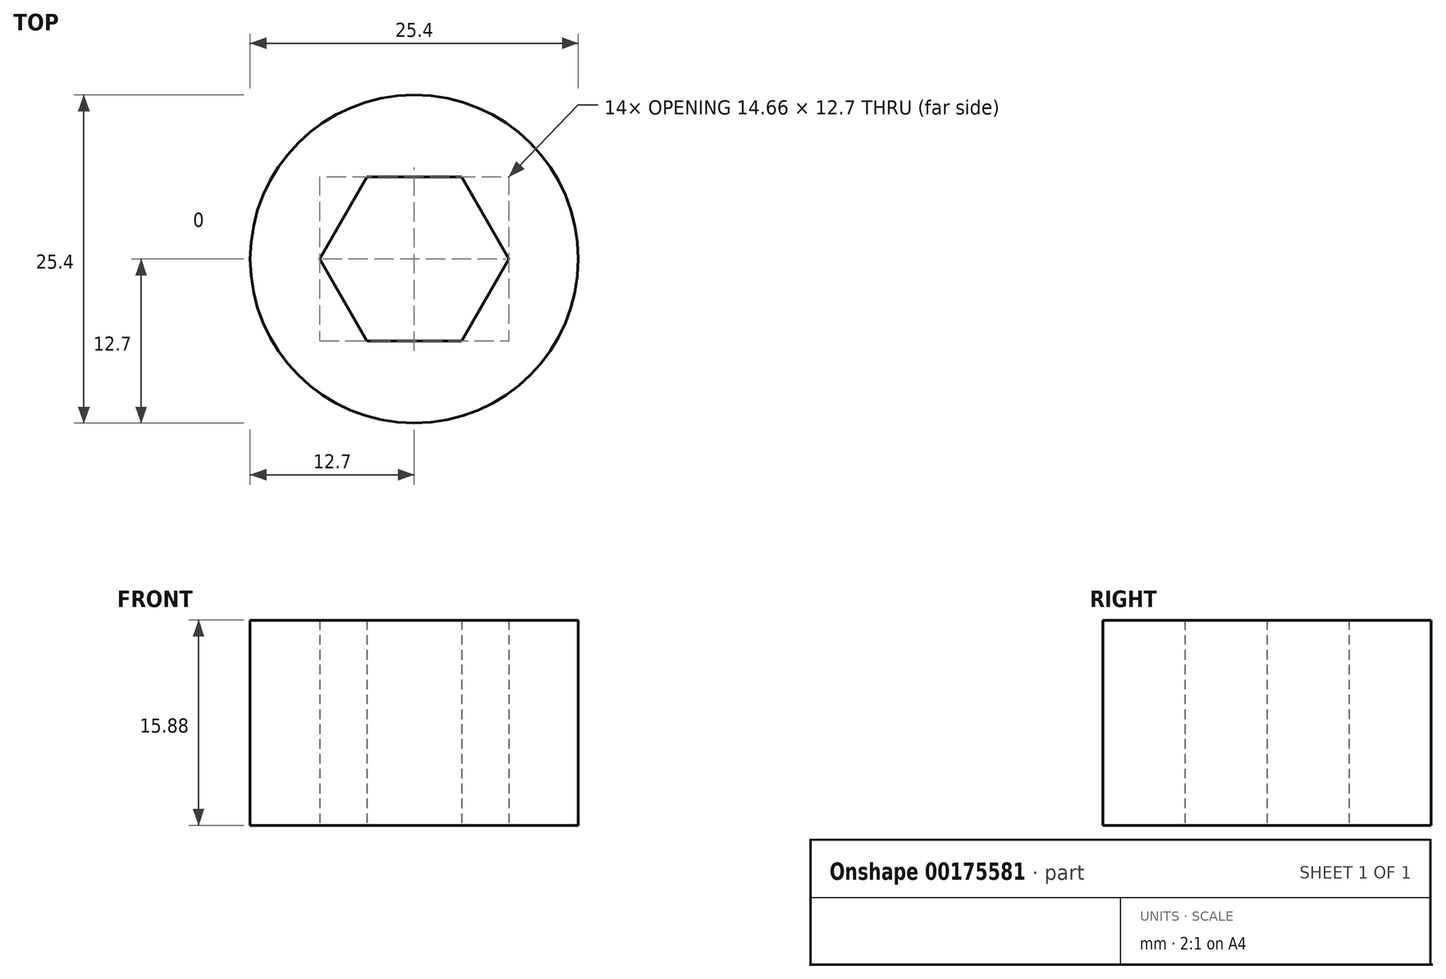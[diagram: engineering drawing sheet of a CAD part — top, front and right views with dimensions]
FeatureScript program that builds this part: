
annotation { "Feature Type Name" : "Feature", "Feature Type Description" : "" }
export const myFeature = defineFeature(function(context is Context, id is Id, definition is map)
    precondition{}
    {
        {
            var Q0;
            Q0=qCreatedBy(makeId("Top.planeOp"),FACE);
            var sketch = newSketch(context, id + "F0", { "sketchPlane" : qUnion([Q0])});
            skCircle(sketch, "E0", {"center": v(0, 0) * mm, "radius": 12.7 * mm});
            skLineSegment(sketch, "E1.0", {"start": v(3.67, -6.35) * mm, "end": v(-3.67, -6.35) * mm});
            skLineSegment(sketch, "E1.1", {"start": v(-3.67, -6.35) * mm, "end": v(-7.33, 0) * mm});
            skLineSegment(sketch, "E1.2", {"start": v(-7.33, 0) * mm, "end": v(-3.67, 6.35) * mm});
            skLineSegment(sketch, "E1.3", {"start": v(-3.67, 6.35) * mm, "end": v(3.67, 6.35) * mm});
            skLineSegment(sketch, "E1.4", {"start": v(3.67, 6.35) * mm, "end": v(7.33, 0) * mm});
            skLineSegment(sketch, "E1.5", {"start": v(7.33, 0) * mm, "end": v(3.67, -6.35) * mm});
            skPoint(sketch, "E1.0.midPoint", {"position": v(0, -6.35) * mm});
            skSolve(sketch);
        }
        {
            var Q0;
            Q0 = qSketchRegion(id + "F0", true);
            extrude(context, id + "F1", {"entities" : qUnion([Q0]), "depth" : 15.88 * mm});
        }
    });
